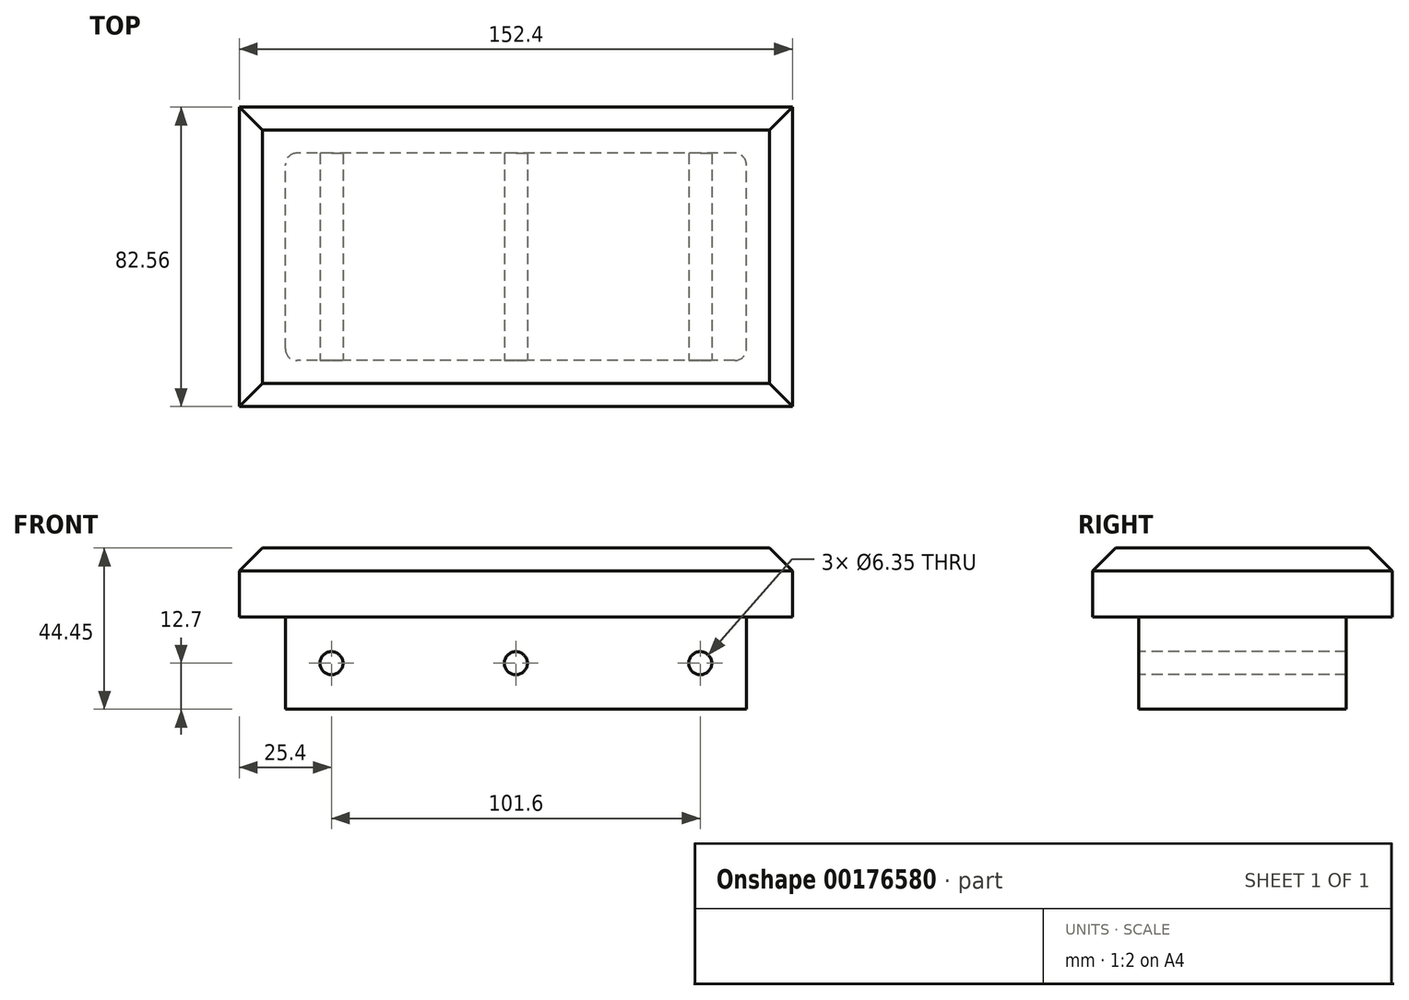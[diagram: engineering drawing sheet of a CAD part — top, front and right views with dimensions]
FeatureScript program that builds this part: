
annotation { "Feature Type Name" : "Feature", "Feature Type Description" : "" }
export const myFeature = defineFeature(function(context is Context, id is Id, definition is map)
    precondition{}
    {
        {
            var Q0;
            Q0=qCreatedBy(makeId("Top.planeOp"),FACE);
            var sketch = newSketch(context, id + "F0", { "sketchPlane" : qUnion([Q0])});
            skLineSegment(sketch, "E0.bottom", {"start": v(76.2, 41.28) * mm, "end": v(-76.2, 41.28) * mm});
            skLineSegment(sketch, "E0.top", {"start": v(76.2, -41.27) * mm, "end": v(-76.2, -41.27) * mm});
            skLineSegment(sketch, "E0.left", {"start": v(76.2, 41.28) * mm, "end": v(76.2, -41.27) * mm});
            skLineSegment(sketch, "E0.right", {"start": v(-76.2, 41.28) * mm, "end": v(-76.2, -41.27) * mm});
            skPoint(sketch, "E0.middle", {"position": v(0, 0) * mm});
            skSolve(sketch);
        }
        {
            var Q0;
            Q0 = qSketchRegion(id + "F0", true);
            extrude(context, id + "F1", {"entities" : qUnion([Q0]), "depth" : 19.05 * mm});
        }
        {
            var Q0;
            Q0=makeQuery(id+"F1.opExtrude","CAP_EDGE",EDGE,{"disambiguationData":[OSD([sQuery(id+"F0.wireOp",EDGE,"E0.bottom")])],"isStart":false});
            var Q1;
            Q1=makeQuery(id+"F1.opExtrude","CAP_EDGE",EDGE,{"disambiguationData":[OSD([sQuery(id+"F0.wireOp",EDGE,"E0.right")])],"isStart":false});
            var Q2;
            Q2=makeQuery(id+"F1.opExtrude","CAP_EDGE",EDGE,{"disambiguationData":[OSD([sQuery(id+"F0.wireOp",EDGE,"E0.top")])],"isStart":false});
            var Q3;
            Q3=makeQuery(id+"F1.opExtrude","CAP_EDGE",EDGE,{"disambiguationData":[OSD([sQuery(id+"F0.wireOp",EDGE,"E0.left")])],"isStart":false});
            chamfer(context, id + "F2", {"entities" : qUnion([Q0, Q1, Q2, Q3]), "width" : 6.35 * mm, "tangentPropagation" : true});
        }
        {
            var Q0;
            Q0=makeQuery(id+"F1.opExtrude","CAP_FACE",FACE,{"disambiguationData":[OSD([sQuery(id+"F0.wireOp",EDGE,"E0.bottom"),sQuery(id+"F0.wireOp",EDGE,"E0.top"),sQuery(id+"F0.wireOp",EDGE,"E0.left"),sQuery(id+"F0.wireOp",EDGE,"E0.right")])],"isStart":true});
            var sketch = newSketch(context, id + "F3", { "sketchPlane" : qUnion([Q0])});
            skLineSegment(sketch, "E1.bottom", {"start": v(63.5, 28.58) * mm, "end": v(-63.5, 28.58) * mm});
            skLineSegment(sketch, "E1.top", {"start": v(63.5, -28.58) * mm, "end": v(-63.5, -28.58) * mm});
            skLineSegment(sketch, "E1.left", {"start": v(63.5, 28.58) * mm, "end": v(63.5, -28.58) * mm});
            skLineSegment(sketch, "E1.right", {"start": v(-63.5, 28.58) * mm, "end": v(-63.5, -28.58) * mm});
            skPoint(sketch, "E1.middle", {"position": v(0, 0) * mm});
            skSolve(sketch);
        }
        {
            var Q0;
            Q0 = qSketchRegion(id + "F3", true);
            extrude(context, id + "F4", {"entities" : qUnion([Q0]), "operationType" : NewBodyOperationType.ADD, "depth" : 25.4 * mm});
        }
        {
            var Q0;
            Q0=makeQuery(id+"F4.opExtrude","SWEPT_FACE",FACE,{"disambiguationData":[OSD([sQuery(id+"F3.wireOp",EDGE,"E1.bottom")])]});
            var sketch = newSketch(context, id + "F5", { "sketchPlane" : qUnion([Q0])});
            skLineSegment(sketch, "E2", {"start": v(-63.5, -25.4) * mm, "end": v(-63.5, -12.7) * mm, "construction": true});
            skPoint(sketch, "E3.endSnap0", {"position": v(63.5, -12.7) * mm});
            skLineSegment(sketch, "E4", {"start": v(-63.5, -12.7) * mm, "end": v(-50.8, -12.7) * mm, "construction": true});
            skLineSegment(sketch, "E5", {"start": v(-50.8, -12.7) * mm, "end": v(0, -12.7) * mm, "construction": true});
            skLineSegment(sketch, "E6", {"start": v(0, -12.7) * mm, "end": v(50.8, -12.7) * mm, "construction": true});
            skCircle(sketch, "E7", {"center": v(-50.8, -12.7) * mm, "radius": 3.18 * mm});
            skCircle(sketch, "E8", {"center": v(0, -12.7) * mm, "radius": 3.18 * mm});
            skCircle(sketch, "E9", {"center": v(50.8, -12.7) * mm, "radius": 3.18 * mm});
            skSolve(sketch);
        }
        {
            var Q0;
            Q0 = qSketchRegion(id + "F5", true);
            extrude(context, id + "F6", {"entities" : qUnion([Q0]), "operationType" : NewBodyOperationType.REMOVE, "endBound" : BoundingType.THROUGH_ALL, "oppositeDirection" : true, "depth" : 25.4 * mm});
        }
        {
            var Q0;
            Q0=makeQuery(id+"F4.opExtrude","SWEPT_EDGE",EDGE,{"disambiguationData":[OSD([sQuery(id+"F3.wireOp",EDGE,"E1.bottom"),sQuery(id+"F3.wireOp",EDGE,"E1.right")])]});
            var Q1;
            Q1=makeQuery(id+"F4.opExtrude","SWEPT_EDGE",EDGE,{"disambiguationData":[OSD([sQuery(id+"F3.wireOp",EDGE,"E1.bottom"),sQuery(id+"F3.wireOp",EDGE,"E1.left")])]});
            var Q2;
            Q2=makeQuery(id+"F4.opExtrude","SWEPT_EDGE",EDGE,{"disambiguationData":[OSD([sQuery(id+"F3.wireOp",EDGE,"E1.top"),sQuery(id+"F3.wireOp",EDGE,"E1.right")])]});
            var Q3;
            Q3=makeQuery(id+"F4.opExtrude","SWEPT_EDGE",EDGE,{"disambiguationData":[OSD([sQuery(id+"F3.wireOp",EDGE,"E1.top"),sQuery(id+"F3.wireOp",EDGE,"E1.left")])]});
            fillet(context, id + "F7", {"entities" : qUnion([Q0, Q1, Q2, Q3]), "radius" : 3.17 * mm, "tangentPropagation" : true, "allowEdgeOverflow" : false});
        }
    });
